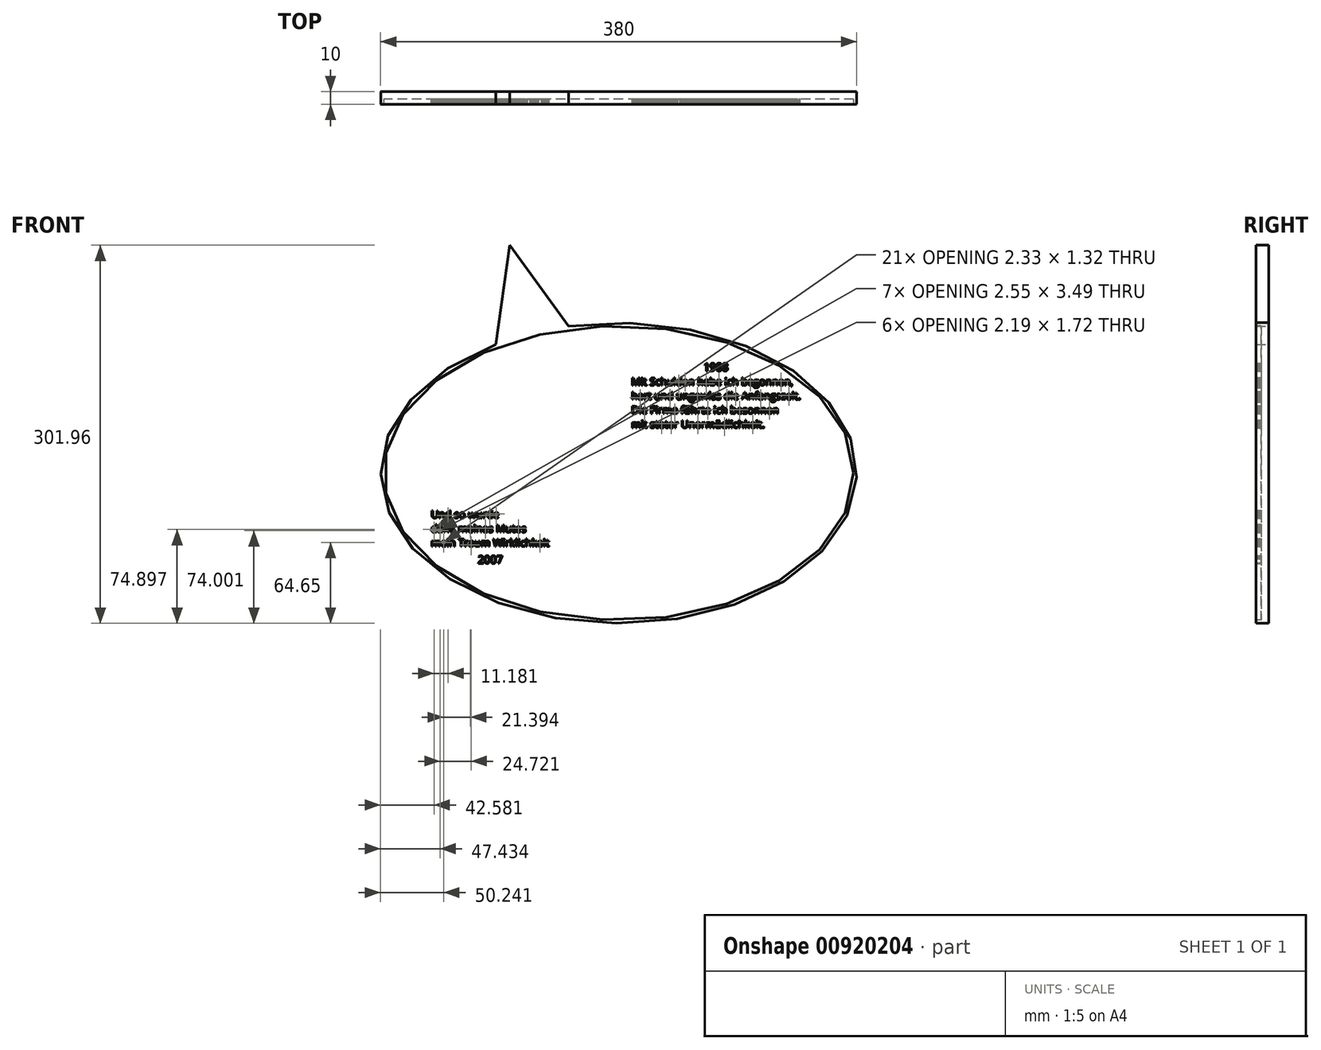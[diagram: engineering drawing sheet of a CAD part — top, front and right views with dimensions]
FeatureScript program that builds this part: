
annotation { "Feature Type Name" : "Feature", "Feature Type Description" : "" }
export const myFeature = defineFeature(function(context is Context, id is Id, definition is map)
    precondition{}
    {
        {
            var Q0;
            Q0=qCreatedBy(makeId("Front.planeOp"),FACE);
            var sketch = newSketch(context, id + "F0", { "sketchPlane" : qUnion([Q0])});
            skEllipse(sketch, "E0", {"center": v(0, 0) * mm, "majorRadius": 190 * mm, "minorRadius": 120 * mm, "majorAxis": v(1, 0)});
            skLineSegment(sketch, "E1", {"start": v(-98.2, 102.73) * mm, "end": v(-87.12, 181.96) * mm});
            skLineSegment(sketch, "E2", {"start": v(-87.12, 181.96) * mm, "end": v(-40, 117.31) * mm});
            skSolve(sketch);
        }
        {
            var Q0;
            Q0 = qSketchRegion(id + "F0", true);
            extrude(context, id + "F1", {"entities" : qUnion([Q0]), "depth" : 10 * mm, "offsetDistance" : 25 * mm});
        }
        {
            var Q0;
            Q0=makeQuery(id+"F1.opExtrude","CAP_FACE",FACE,{"disambiguationData":[OSD([sQuery(id+"F0.wireOp",EDGE,"E0"),sQuery(id+"F0.wireOp",EDGE,"E1"),sQuery(id+"F0.wireOp",EDGE,"E2")])],"isStart":false});
            var sketch = newSketch(context, id + "F2", { "sketchPlane" : qUnion([Q0])});
            skEllipse(sketch, "E3", {"center": v(0, 0) * mm, "majorRadius": 187.5 * mm, "minorRadius": 117.5 * mm, "majorAxis": v(1, 0)});
            skSolve(sketch);
        }
        {
            var Q0;
            Q0 = qSketchRegion(id + "F2", true);
            extrude(context, id + "F3", {"entities" : qUnion([Q0]), "operationType" : NewBodyOperationType.REMOVE, "depth" : -4 * mm, "offsetDistance" : 25 * mm});
        }
        {
            var Q0;
            Q0=makeQuery(id+"F3.boolean.opBoolean","COPY",FACE,{"derivedFrom":makeQuery(id+"F3.opExtrude","CAP_FACE",FACE,{"disambiguationData":[OSD([sQuery(id+"F2.wireOp",EDGE,"E3")])],"isStart":false})});
            var sketch = newSketch(context, id + "F4", { "sketchPlane" : qUnion([Q0])});
            skText(sketch, "E4", { "text": "Mit Schulden habe ich begonnen,\nhart und ungewiss die Anfangszeit.\nDie Firma führte ich besonnen\nmit steter Unermüdlichkeit.", "fontName": "OpenSans-Regular.ttf"});
            skText(sketch, "E5", { "text": "1988", "fontName": "OpenSans-Regular.ttf"});
            skText(sketch, "E6", { "text": "2007", "fontName": "OpenSans-Regular.ttf"});
            skText(sketch, "E7", { "text": "Und so wurde\ndank meines Mutes\nmein Traum Wirklichkeit", "fontName": "OpenSans-Regular.ttf"});
            const initialGuessF4  = {"E4": [0.01, 0.07, 1, 0, 0.006], "E5": [0.06763, 0.0815, 1, 0, 0.00626], "E6": [-0.11243, -0.07226, 1, 0, 0.00626], "E7": [-0.14986, -0.036, 1, 0, 0.006]};
            skSetInitialGuess(sketch, initialGuessF4);
            skSolve(sketch);
        }
        {
            var Q0;
            Q0 = qSketchRegion(id + "F4", true);
            extrude(context, id + "F5", {"entities" : qUnion([Q0]), "depth" : 4 * mm, "offsetDistance" : 25 * mm});
        }
    });
